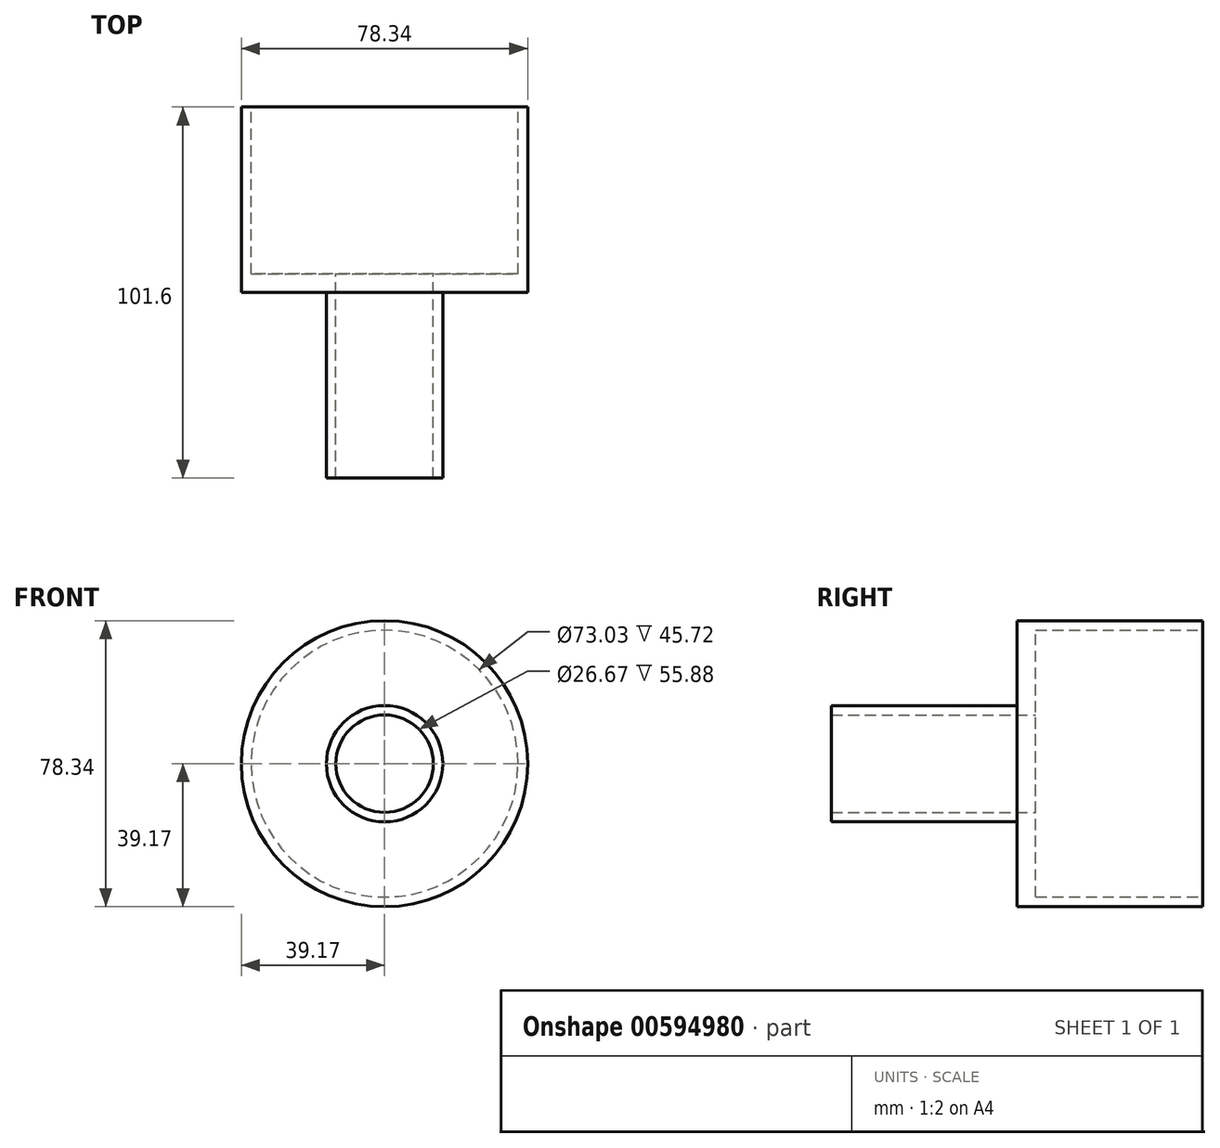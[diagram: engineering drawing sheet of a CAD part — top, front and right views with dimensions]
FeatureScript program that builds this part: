
annotation { "Feature Type Name" : "Feature", "Feature Type Description" : "" }
export const myFeature = defineFeature(function(context is Context, id is Id, definition is map)
    precondition{}
    {
        {
            var Q0;
            Q0=qCreatedBy(makeId("Front.planeOp"),FACE);
            var sketch = newSketch(context, id + "F0", { "sketchPlane" : qUnion([Q0])});
            skCircle(sketch, "E0", {"center": v(0, 0) * mm, "radius": 36.51 * mm});
            skCircle(sketch, "E1", {"center": v(0, 0) * mm, "radius": 39.17 * mm});
            skSolve(sketch);
        }
        {
            var Q0;
            Q0 = qSketchRegion(id + "F0", true);
            extrude(context, id + "F1", {"entities" : qUnion([Q0]), "depth" : 45.72 * mm, "offsetDistance" : 25.4 * mm});
        }
        {
            var Q0;
            Q0=qCreatedBy(makeId("Front.planeOp"),FACE);
            cPlane(context, id + "F2", {"entities" : qUnion([Q0]), "cplaneType" : CPlaneType.OFFSET, "offset" : 45.72 * mm, "width" : 152.4 * mm, "height" : 152.4 * mm});
        }
        {
            var Q0;
            Q0=qCreatedBy(id+"F2.planeOp",FACE);
            var sketch = newSketch(context, id + "F3", { "sketchPlane" : qUnion([Q0])});
            skCircle(sketch, "E2", {"center": v(0, 0) * mm, "radius": 39.17 * mm});
            skCircle(sketch, "E3", {"center": v(0, 0) * mm, "radius": 13.34 * mm});
            skSolve(sketch);
        }
        {
            var Q0;
            Q0 = qSketchRegion(id + "F3", true);
            extrude(context, id + "F4", {"entities" : qUnion([Q0]), "operationType" : NewBodyOperationType.ADD, "depth" : 5.08 * mm, "offsetDistance" : 25.4 * mm});
        }
        {
            var Q0;
            Q0=qCreatedBy(id+"F2.planeOp",FACE);
            cPlane(context, id + "F5", {"entities" : qUnion([Q0]), "cplaneType" : CPlaneType.OFFSET, "offset" : 5.08 * mm, "width" : 152.4 * mm, "height" : 152.4 * mm});
        }
        {
            var Q0;
            Q0=qCreatedBy(id+"F5.planeOp",FACE);
            var sketch = newSketch(context, id + "F6", { "sketchPlane" : qUnion([Q0])});
            skCircle(sketch, "E4", {"center": v(0, 0) * mm, "radius": 13.34 * mm});
            skCircle(sketch, "E5", {"center": v(0, 0) * mm, "radius": 15.93 * mm});
            skSolve(sketch);
        }
        {
            var Q0;
            Q0 = qSketchRegion(id + "F6", true);
            extrude(context, id + "F7", {"entities" : qUnion([Q0]), "operationType" : NewBodyOperationType.ADD, "depth" : 50.8 * mm, "offsetDistance" : 25.4 * mm});
        }
    });
